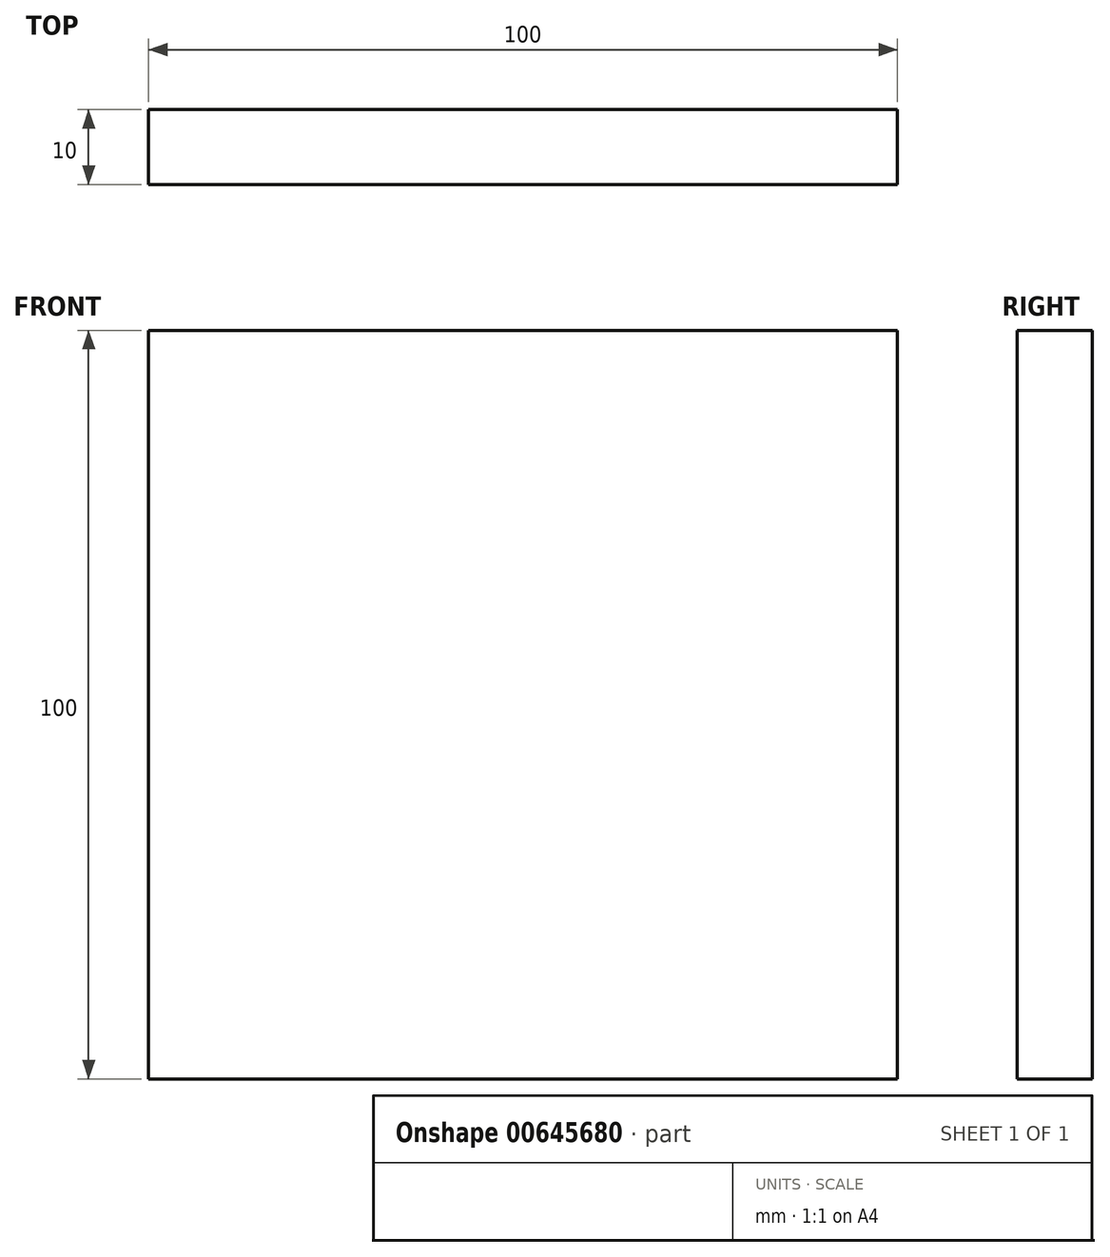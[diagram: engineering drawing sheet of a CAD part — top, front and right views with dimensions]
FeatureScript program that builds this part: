
annotation { "Feature Type Name" : "Feature", "Feature Type Description" : "" }
export const myFeature = defineFeature(function(context is Context, id is Id, definition is map)
    precondition{}
    {
        {
            var Q0;
            Q0=qCreatedBy(makeId("Front.planeOp"),FACE);
            var sketch = newSketch(context, id + "F0", { "sketchPlane" : qUnion([Q0])});
            skLineSegment(sketch, "E0.bottom", {"start": v(-83.16, 60.61) * mm, "end": v(16.84, 60.61) * mm});
            skLineSegment(sketch, "E0.top", {"start": v(-83.16, -39.39) * mm, "end": v(16.84, -39.39) * mm});
            skLineSegment(sketch, "E0.left", {"start": v(-83.16, 60.61) * mm, "end": v(-83.16, -39.39) * mm});
            skLineSegment(sketch, "E0.right", {"start": v(16.84, 60.61) * mm, "end": v(16.84, -39.39) * mm});
            skSolve(sketch);
        }
        {
            var Q0;
            Q0 = qSketchRegion(id + "F0", true);
            extrude(context, id + "F1", {"entities" : qUnion([Q0]), "depth" : 10 * mm, "offsetDistance" : 25 * mm});
        }
    });
